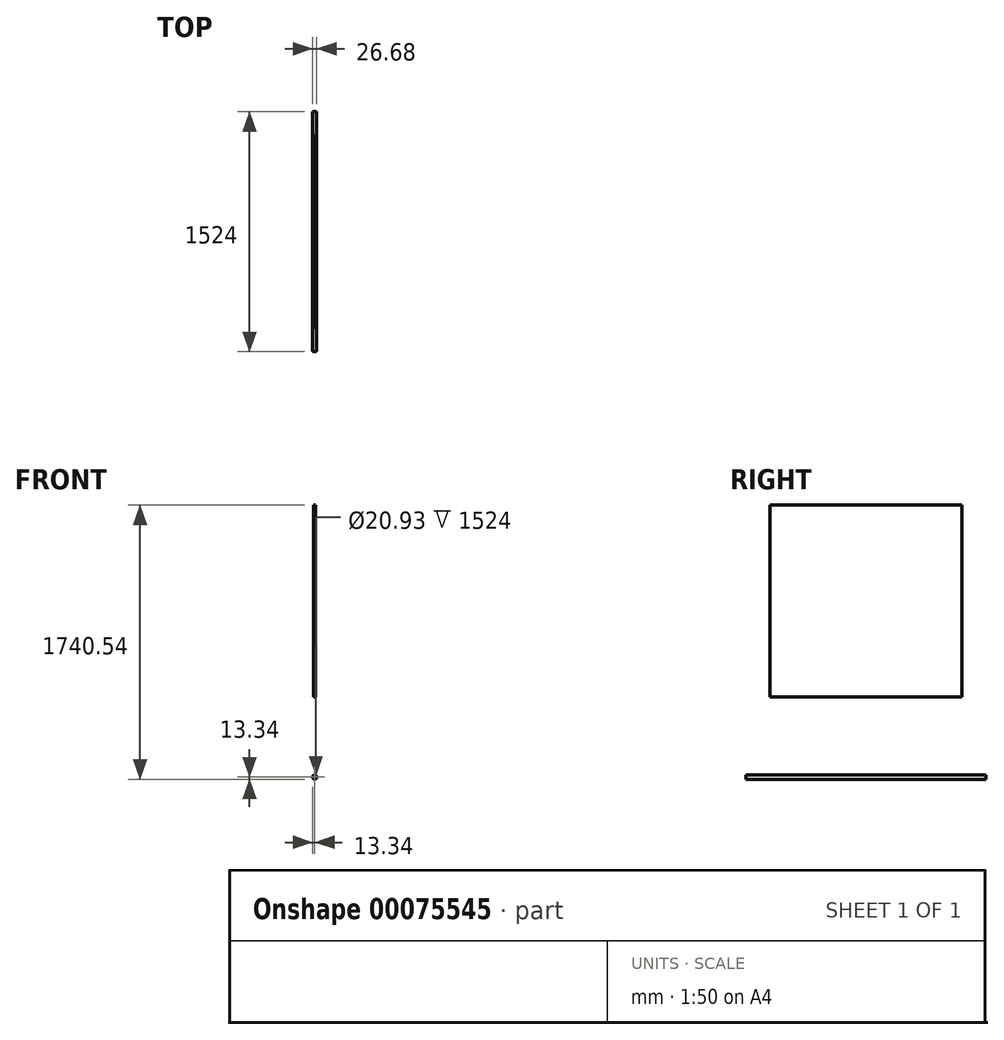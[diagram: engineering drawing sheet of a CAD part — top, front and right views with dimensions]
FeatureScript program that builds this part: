
annotation { "Feature Type Name" : "Feature", "Feature Type Description" : "" }
export const myFeature = defineFeature(function(context is Context, id is Id, definition is map)
    precondition{}
    {
        {
            var Q0;
            Q0=qCreatedBy(makeId("Front.planeOp"),FACE);
            var sketch = newSketch(context, id + "F0", { "sketchPlane" : qUnion([Q0])});
            skCircle(sketch, "E0", {"center": v(0, 0) * mm, "radius": 13.34 * mm});
            skCircle(sketch, "E1", {"center": v(0, 0) * mm, "radius": 10.46 * mm});
            skSolve(sketch);
        }
        {
            var Q0;
            Q0=makeQuery(id+"F0.imprint","IMPRINT",FACE,{"disambiguationData":[TD([[makeQuery(id+"F0.imprint","IMPRINT",EDGE,{"derivedFrom":sQuery(id+"F0.wireOp",EDGE,"E0")}),1.0]])]});
            extrude(context, id + "F1", {"entities" : qUnion([Q0]), "endBound" : BoundingType.SYMMETRIC, "depth" : 1524 * mm});
        }
        {
            var Q0;
            Q0=qCreatedBy(makeId("Right.planeOp"),FACE);
            var sketch = newSketch(context, id + "F2", { "sketchPlane" : qUnion([Q0])});
            skLineSegment(sketch, "E2.rect.bottom", {"start": v(-609.6, 508) * mm, "end": v(609.6, 508) * mm});
            skLineSegment(sketch, "E2.rect.top", {"start": v(-609.6, 1727.2) * mm, "end": v(609.6, 1727.2) * mm});
            skLineSegment(sketch, "E2.rect.left", {"start": v(-609.6, 508) * mm, "end": v(-609.6, 1727.2) * mm});
            skLineSegment(sketch, "E2.rect.right", {"start": v(609.6, 508) * mm, "end": v(609.6, 1727.2) * mm});
            skPoint(sketch, "E2.rect.middle", {"position": v(0, 1117.6) * mm});
            skSolve(sketch);
        }
        {
            var Q0;
            Q0=makeQuery(id+"F2.imprint","IMPRINT",FACE,{"disambiguationData":[TD([[makeQuery(id+"F2.imprint","IMPRINT",EDGE,{"derivedFrom":sQuery(id+"F2.wireOp",EDGE,"E2.rect.bottom")}),1.0]])]});
            extrude(context, id + "F3", {"entities" : qUnion([Q0]), "endBound" : BoundingType.SYMMETRIC, "depth" : 12.7 * mm});
        }
    });
